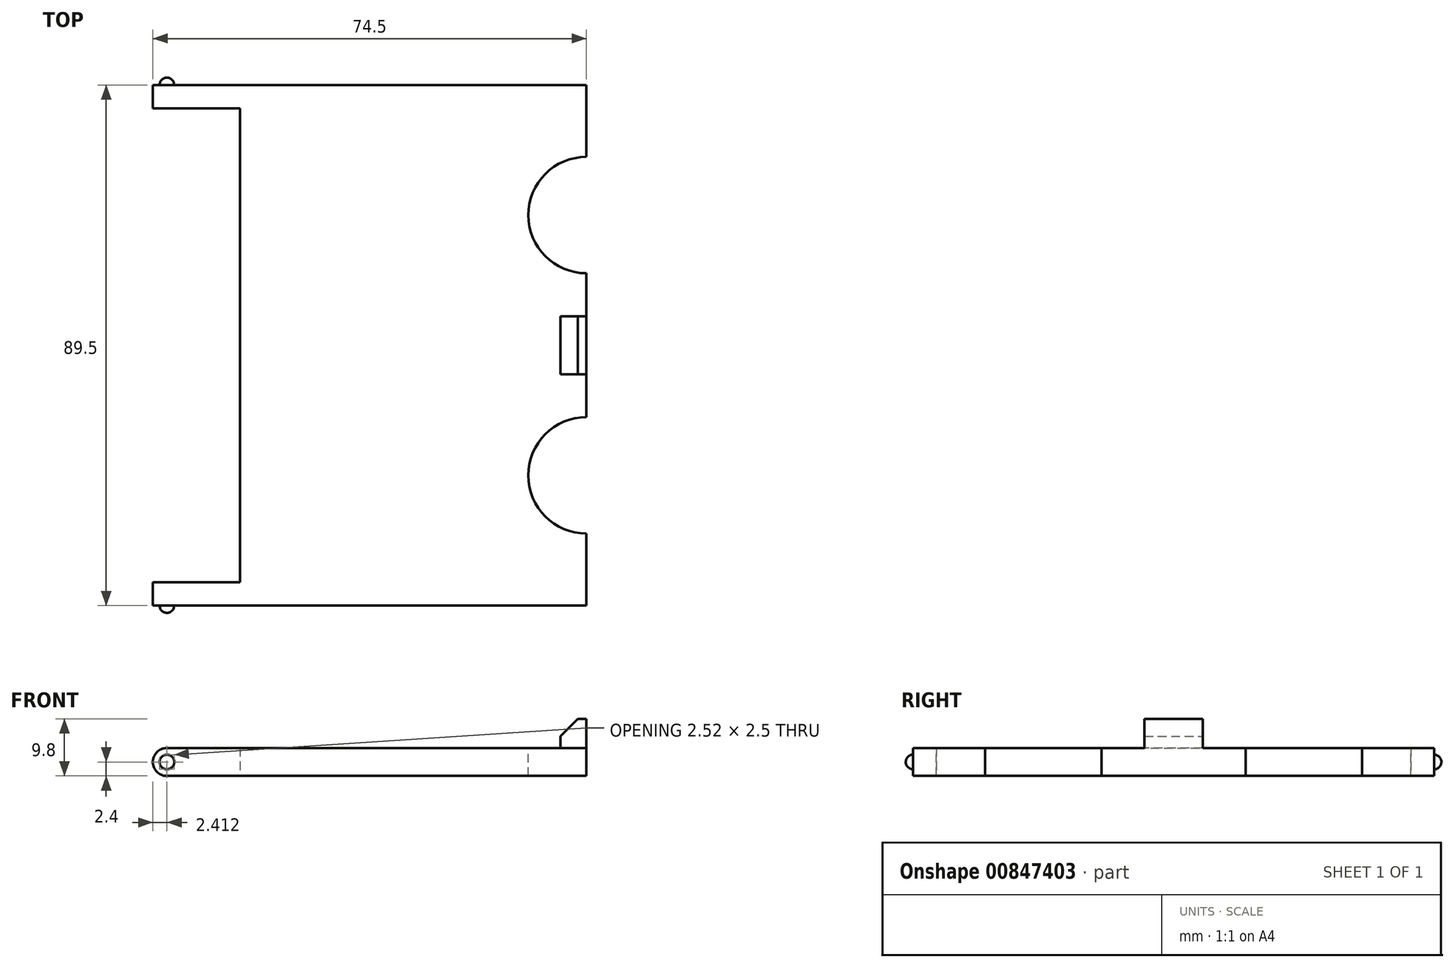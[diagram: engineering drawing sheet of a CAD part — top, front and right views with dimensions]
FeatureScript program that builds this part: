
annotation { "Feature Type Name" : "Feature", "Feature Type Description" : "" }
export const myFeature = defineFeature(function(context is Context, id is Id, definition is map)
    precondition{}
    {
        {
            var Q0;
            Q0=qCreatedBy(makeId("Top.planeOp"),FACE);
            var sketch = newSketch(context, id + "F0", { "sketchPlane" : qUnion([Q0])});
            skLineSegment(sketch, "E0.bottom", {"start": v(-37.25, -44.75) * mm, "end": v(37.25, -44.75) * mm});
            skLineSegment(sketch, "E0.top", {"start": v(-37.25, 44.75) * mm, "end": v(37.25, 44.75) * mm});
            skLineSegment(sketch, "E0.left", {"start": v(-37.25, -44.75) * mm, "end": v(-37.25, -40.75) * mm});
            skLineSegment(sketch, "E0.right", {"start": v(37.25, -44.75) * mm, "end": v(37.25, 44.75) * mm});
            skPoint(sketch, "E0.middle", {"position": v(0, 0) * mm});
            skLineSegment(sketch, "E1.bottom", {"start": v(-37.25, -40.75) * mm, "end": v(-22.25, -40.75) * mm});
            skLineSegment(sketch, "E1.top", {"start": v(-37.25, 40.75) * mm, "end": v(-22.25, 40.75) * mm});
            skLineSegment(sketch, "E1.right", {"start": v(-22.25, -40.75) * mm, "end": v(-22.25, 40.75) * mm});
            skLineSegment(sketch, "E2.trimOffspring", {"start": v(-37.25, 40.75) * mm, "end": v(-37.25, 44.75) * mm});
            skSolve(sketch);
        }
        {
            var Q0;
            Q0=qSketchRegion(id+"F0",true);
            extrude(context, id + "F1", {"entities" : qUnion([Q0]), "depth" : 4.8 * mm, "offsetDistance" : 25 * mm});
        }
        {
            var Q0;
            Q0=makeQuery(id+"F1.opExtrude","SWEPT_FACE",FACE,{"disambiguationData":[OSD([sQuery(id+"F0.wireOp",EDGE,"E0.bottom")])]});
            var sketch = newSketch(context, id + "F2", { "sketchPlane" : qUnion([Q0])});
            skCircle(sketch, "E3", {"center": v(-34.85, 2.4) * mm, "radius": 2.4 * mm});
            skArc(sketch, "E4", {"start": v(-34.84, 3.65) * mm, "mid": v(-36.1, 2.4) * mm, "end": v(-34.84, 1.15) * mm});
            skLineSegment(sketch, "E5", {"start": v(-34.84, 3.65) * mm, "end": v(-34.84, 1.15) * mm});
            skSolve(sketch);
        }
        {
            var Q0;
            Q0=makeQuery(id+"F2.imprint","IMPRINT",FACE,{"disambiguationData":[TD([[makeQuery(id+"F2.imprint","IMPRINT",EDGE,{"derivedFrom":sQuery(id+"F2.wireOp",EDGE,"E4")}),1.0]])]});
            var Q1;
            Q1=sQuery(id+"F2.wireOp",EDGE,"E5");
            revolve(context, id + "F3", {"operationType" : NewBodyOperationType.ADD, "surfaceOperationType" : NewSurfaceOperationType.NEW, "entities" : qUnion([Q0]), "axis" : qUnion([Q1]), "revolveType" : RevolveType.FULL});
        }
        {
            var Q0;
            Q0=makeQuery(id+"F1.opExtrude","SWEPT_BODY",BODY,{"disambiguationData":[OSD([sQuery(id+"F0.wireOp",EDGE,"E0.bottom"),sQuery(id+"F0.wireOp",EDGE,"E0.top"),sQuery(id+"F0.wireOp",EDGE,"E0.left"),sQuery(id+"F0.wireOp",EDGE,"E0.right"),sQuery(id+"F0.wireOp",EDGE,"E1.bottom"),sQuery(id+"F0.wireOp",EDGE,"E1.top"),sQuery(id+"F0.wireOp",EDGE,"E1.right"),sQuery(id+"F0.wireOp",EDGE,"E2.trimOffspring")])]});
            var Q1;
            Q1=qCreatedBy(makeId("Front.planeOp"),FACE);
            mirror(context, id + "F4", {"operationType" : NewBodyOperationType.ADD, "entities" : qUnion([Q0]), "mirrorPlane" : qUnion([Q1])});
        }
        {
            var Q0;
            Q0=makeQuery(id+"F1.opExtrude","CAP_FACE",FACE,{"disambiguationData":[OSD([sQuery(id+"F0.wireOp",EDGE,"E0.bottom"),sQuery(id+"F0.wireOp",EDGE,"E0.top"),sQuery(id+"F0.wireOp",EDGE,"E0.left"),sQuery(id+"F0.wireOp",EDGE,"E0.right"),sQuery(id+"F0.wireOp",EDGE,"E1.bottom"),sQuery(id+"F0.wireOp",EDGE,"E1.top"),sQuery(id+"F0.wireOp",EDGE,"E1.right"),sQuery(id+"F0.wireOp",EDGE,"E2.trimOffspring")])],"isStart":false});
            var sketch = newSketch(context, id + "F5", { "sketchPlane" : qUnion([Q0])});
            skPoint(sketch, "E6", {"position": v(37.25, 22.37) * mm});
            skCircle(sketch, "E7", {"center": v(37.25, 22.37) * mm, "radius": 10 * mm});
            skCircle(sketch, "E8.MirrorC", {"center": v(37.25, -22.37) * mm, "radius": 10 * mm});
            skSolve(sketch);
        }
        {
            var Q0;
            Q0=qSketchRegion(id+"F5",true);
            extrude(context, id + "F6", {"entities" : qUnion([Q0]), "operationType" : NewBodyOperationType.REMOVE, "endBound" : BoundingType.THROUGH_ALL, "oppositeDirection" : true, "depth" : 25 * mm, "offsetDistance" : 25 * mm});
        }
        {
            var Q0;
            Q0=makeQuery(id+"F1.opExtrude","CAP_FACE",FACE,{"disambiguationData":[OSD([sQuery(id+"F0.wireOp",EDGE,"E0.bottom"),sQuery(id+"F0.wireOp",EDGE,"E0.top"),sQuery(id+"F0.wireOp",EDGE,"E0.left"),sQuery(id+"F0.wireOp",EDGE,"E0.right"),sQuery(id+"F0.wireOp",EDGE,"E1.bottom"),sQuery(id+"F0.wireOp",EDGE,"E1.top"),sQuery(id+"F0.wireOp",EDGE,"E1.right"),sQuery(id+"F0.wireOp",EDGE,"E2.trimOffspring")])],"isStart":false});
            var sketch = newSketch(context, id + "F7", { "sketchPlane" : qUnion([Q0])});
            skLineSegment(sketch, "E9.bottom", {"start": v(37.25, 5) * mm, "end": v(32.75, 5) * mm});
            skLineSegment(sketch, "E9.top", {"start": v(37.25, -5) * mm, "end": v(32.75, -5) * mm});
            skLineSegment(sketch, "E9.left", {"start": v(37.25, 5) * mm, "end": v(37.25, -5) * mm});
            skLineSegment(sketch, "E9.right", {"start": v(32.75, 5) * mm, "end": v(32.75, -5) * mm});
            skPoint(sketch, "E10", {"position": v(32.75, 0) * mm});
            skSolve(sketch);
        }
        {
            var Q0;
            Q0=makeQuery(id+"F7.imprint","IMPRINT",FACE,{"disambiguationData":[TD([[makeQuery(id+"F7.imprint","IMPRINT",EDGE,{"derivedFrom":sQuery(id+"F7.wireOp",EDGE,"E9.bottom")}),1.0]])]});
            extrude(context, id + "F8", {"entities" : qUnion([Q0]), "operationType" : NewBodyOperationType.ADD, "depth" : 5 * mm, "offsetDistance" : 25 * mm});
        }
        {
            var Q0;
            Q0=makeQuery(id+"F8.opExtrude","CAP_EDGE",EDGE,{"disambiguationData":[OSD([sQuery(id+"F7.wireOp",EDGE,"E9.right")])],"isStart":false});
            chamfer(context, id + "F9", {"entities" : qUnion([Q0]), "width" : 3 * mm, "tangentPropagation" : true});
        }
        {
            var Q0;
            {var subQ0=sQuery(id+"F2.wireOp",EDGE,"E3");var subQ1=sQuery(id+"F0.wireOp",EDGE,"E0.bottom");var subQ4=makeQuery(id+"F1.opExtrude","CAP_EDGE",EDGE,{"disambiguationData":[OSD([subQ1])],"isStart":false});var subQ5=makeQuery(id+"F2.imprint","INTERSECT",VERTEX,{"derivedFrom":[subQ4,subQ0]});Q0=makeQuery(id+"F2.imprint","IMPRINT",FACE,{"disambiguationData":[TD([[makeQuery(id+"F2.imprint","IMPRINT",EDGE,{"disambiguationData":[TD([[subQ5,-1.0]])],"derivedFrom":subQ0}),-1.0]])]});}
            var Q1;
            {var subQ0=sQuery(id+"F2.wireOp",EDGE,"E3");var subQ1=sQuery(id+"F0.wireOp",EDGE,"E0.bottom");var subQ4=makeQuery(id+"F1.opExtrude","CAP_EDGE",EDGE,{"disambiguationData":[OSD([subQ1])],"isStart":true});var subQ5=makeQuery(id+"F2.imprint","INTERSECT",VERTEX,{"derivedFrom":[subQ4,subQ0]});Q1=makeQuery(id+"F2.imprint","IMPRINT",FACE,{"disambiguationData":[TD([[makeQuery(id+"F2.imprint","IMPRINT",EDGE,{"disambiguationData":[TD([[subQ5,1.0]])],"derivedFrom":subQ0}),-1.0]])]});}
            extrude(context, id + "F10", {"entities" : qUnion([Q0, Q1]), "operationType" : NewBodyOperationType.REMOVE, "endBound" : BoundingType.THROUGH_ALL, "oppositeDirection" : true, "depth" : 25 * mm, "offsetDistance" : 25 * mm});
        }
    });
